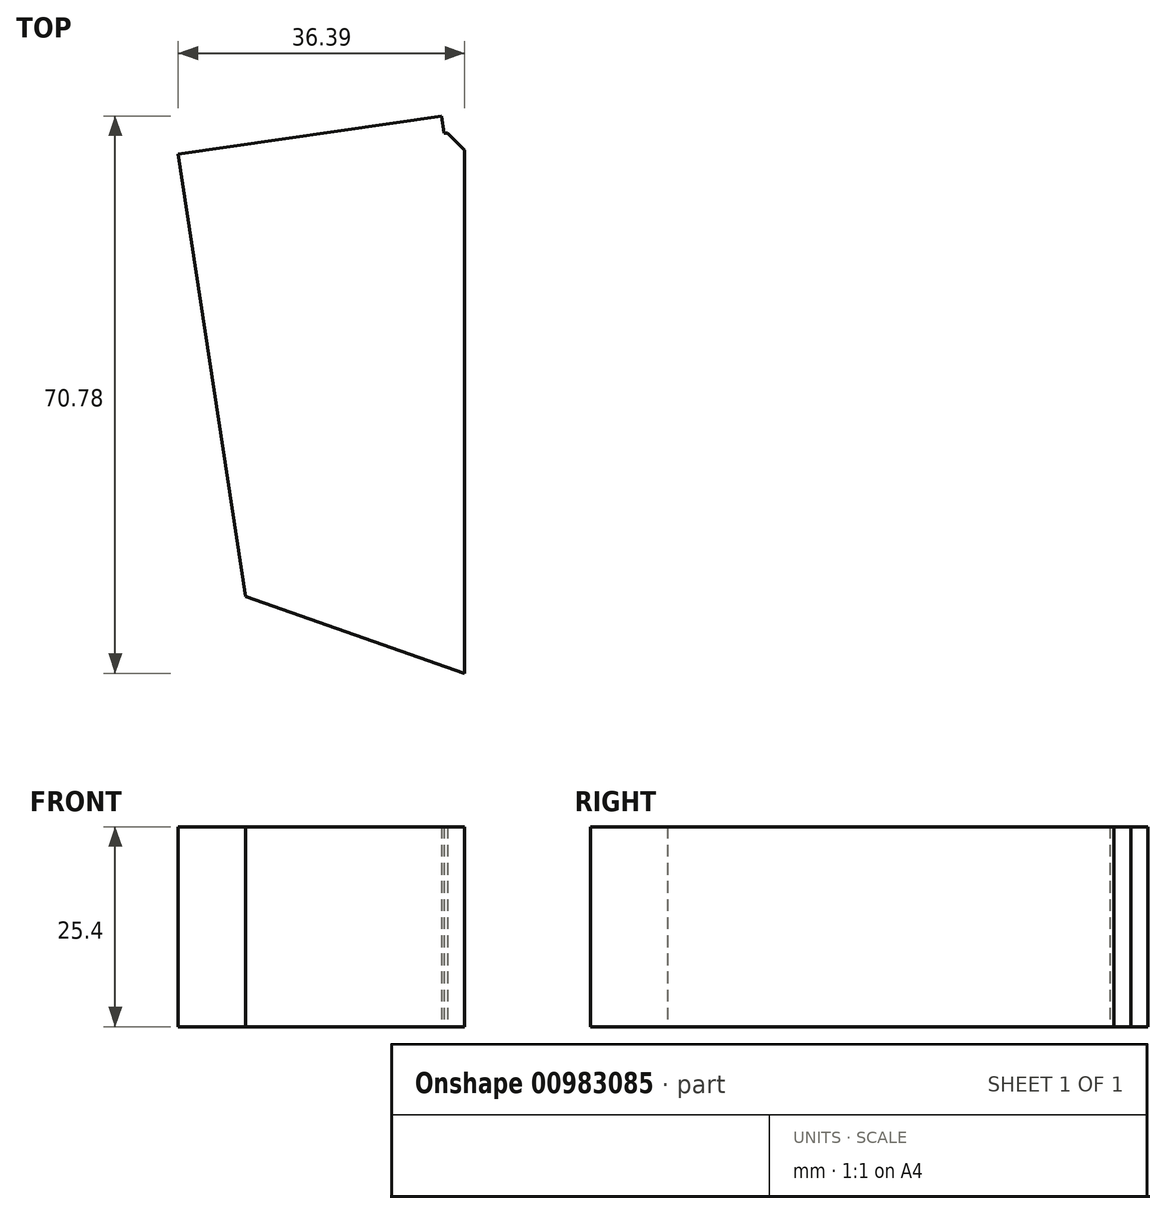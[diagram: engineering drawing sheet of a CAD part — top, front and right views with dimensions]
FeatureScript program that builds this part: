
annotation { "Feature Type Name" : "Feature", "Feature Type Description" : "" }
export const myFeature = defineFeature(function(context is Context, id is Id, definition is map)
    precondition{}
    {
        {
            var Q0;
            Q0=qCreatedBy(makeId("Top.planeOp"),FACE);
            var sketch = newSketch(context, id + "F0", { "sketchPlane" : qUnion([Q0])});
            skLineSegment(sketch, "E0", {"start": v(39.05, 32.74) * mm, "end": v(39.05, -33.74) * mm});
            skLineSegment(sketch, "E1", {"start": v(39.05, -33.74) * mm, "end": v(11.19, -24.02) * mm});
            skLineSegment(sketch, "E2", {"start": v(11.19, -24.02) * mm, "end": v(2.66, 32.2) * mm});
            skLineSegment(sketch, "E3", {"start": v(2.66, 32.2) * mm, "end": v(36.12, 37.04) * mm});
            skLineSegment(sketch, "E4", {"start": v(39.05, 32.74) * mm, "end": v(36.5, 35.2) * mm});
            skLineSegment(sketch, "E5", {"start": v(36.12, 37.04) * mm, "end": v(36.45, 34.86) * mm});
            skLineSegment(sketch, "E6", {"start": v(36.45, 34.86) * mm, "end": v(40.18, 34.86) * mm});
            skSolve(sketch);
        }
        {
            var Q0;
            Q0 = qSketchRegion(id + "F0", true);
            extrude(context, id + "F1", {"entities" : qUnion([Q0]), "depth" : 25.4 * mm, "offsetDistance" : 25.4 * mm});
        }
    });
